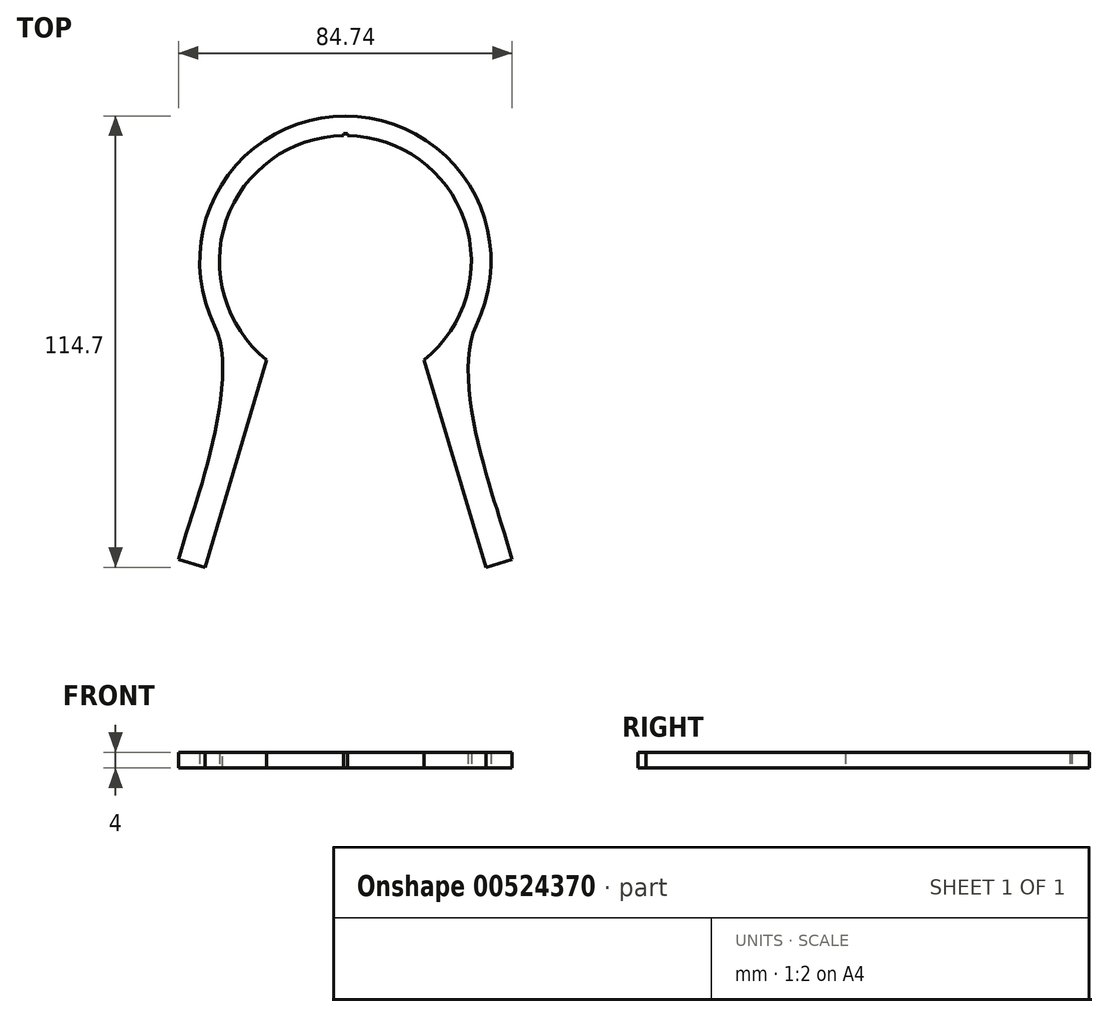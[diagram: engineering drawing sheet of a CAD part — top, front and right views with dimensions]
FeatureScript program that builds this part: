
annotation { "Feature Type Name" : "Feature", "Feature Type Description" : "" }
export const myFeature = defineFeature(function(context is Context, id is Id, definition is map)
    precondition{}
    {
        {
            assignVariable(context, id + "F0", {"name" : "wrenchThickness", "anyValue" : 4});
        }
        {
            var Q0;
            Q0=qCreatedBy(makeId("Top.planeOp"),FACE);
            var sketch = newSketch(context, id + "F1", { "sketchPlane" : qUnion([Q0])});
            skArc(sketch, "E0", {"start": v(33.2, -16.34) * mm, "mid": v(0, 37) * mm, "end": v(-33.2, -16.34) * mm});
            skArc(sketch, "E1", {"start": v(20, -24.98) * mm, "mid": v(0, 32) * mm, "end": v(-20, -24.98) * mm});
            skLineSegment(sketch, "E2", {"start": v(20, -24.98) * mm, "end": v(35.66, -77.7) * mm});
            skLineSegment(sketch, "E3", {"start": v(-20, -24.98) * mm, "end": v(-35.66, -77.7) * mm});
            skLineSegment(sketch, "E4", {"start": v(0, -3.1) * mm, "end": v(0, -86.78) * mm, "construction": true});
            skLineSegment(sketch, "E5", {"start": v(20, -24.98) * mm, "end": v(0, -24.98) * mm, "construction": true});
            skLineSegment(sketch, "E6", {"start": v(0, -24.98) * mm, "end": v(-20, -24.98) * mm, "construction": true});
            skLineSegment(sketch, "E7", {"start": v(-35.66, -77.7) * mm, "end": v(0, -77.7) * mm, "construction": true});
            skLineSegment(sketch, "E8", {"start": v(0, -77.7) * mm, "end": v(35.66, -77.7) * mm, "construction": true});
            skLineSegment(sketch, "E9", {"start": v(-35.66, -77.7) * mm, "end": v(-42.37, -75.7) * mm});
            skLineSegment(sketch, "E10", {"start": v(-42.37, -75.7) * mm, "end": v(-40.41, -69.1) * mm});
            skFitSpline(sketch, "E11", {"points": [v(-40.41, -69.1) * mm, v(-33.2, -16.34) * mm], "startDerivative": vector(7.4, 24.9) * mm, "endDerivative": vector(-19.78, 40.2) * mm});
            skFitSpline(sketch, "E12.MirrorCS", {"points": [v(40.41, -69.1) * mm, v(33.2, -16.34) * mm], "startDerivative": vector(-7.4, 24.9) * mm, "endDerivative": vector(19.78, 40.2) * mm});
            skLineSegment(sketch, "E13.MirrorCS", {"start": v(42.37, -75.7) * mm, "end": v(40.41, -69.1) * mm});
            skLineSegment(sketch, "E14.MirrorCS", {"start": v(35.66, -77.7) * mm, "end": v(42.37, -75.7) * mm});
            skSolve(sketch);
        }
        {
            var Q0;
            Q0 = qSketchRegion(id + "F1", true);
            extrude(context, id + "F2", {"entities" : qUnion([Q0]), "depth" : (getVariable(context, 'wrenchThickness')) * mm, "offsetDistance" : 25 * mm});
        }
        {
            var Q0;
            Q0=qCreatedBy(makeId("Top.planeOp"),FACE);
            var sketch = newSketch(context, id + "F3", { "sketchPlane" : qUnion([Q0])});
            skArc(sketch, "E15.0", {"start": v(0.5, 32) * mm, "mid": v(0, 32) * mm, "end": v(-0.5, 32) * mm});
            skLineSegment(sketch, "E16", {"start": v(0, 0) * mm, "end": v(0, 80.2) * mm, "construction": true});
            skLineSegment(sketch, "E17", {"start": v(-0.5, 32) * mm, "end": v(-0.5, 32.5) * mm});
            skLineSegment(sketch, "E18", {"start": v(-0.5, 32.5) * mm, "end": v(0, 32.5) * mm});
            skLineSegment(sketch, "E19", {"start": v(0, 32.5) * mm, "end": v(0.5, 32.5) * mm});
            skLineSegment(sketch, "E20", {"start": v(0.5, 32.5) * mm, "end": v(0.5, 32) * mm});
            skPoint(sketch, "E21.orphan", {"position": v(-20, -24.98) * mm});
            skPoint(sketch, "E22.orphan", {"position": v(20, -24.98) * mm});
            skSolve(sketch);
        }
        {
            var Q0;
            Q0 = qSketchRegion(id + "F3", true);
            extrude(context, id + "F4", {"entities" : qUnion([Q0]), "operationType" : NewBodyOperationType.REMOVE, "endBound" : BoundingType.THROUGH_ALL, "depth" : 25 * mm, "offsetDistance" : 25 * mm});
        }
    });
